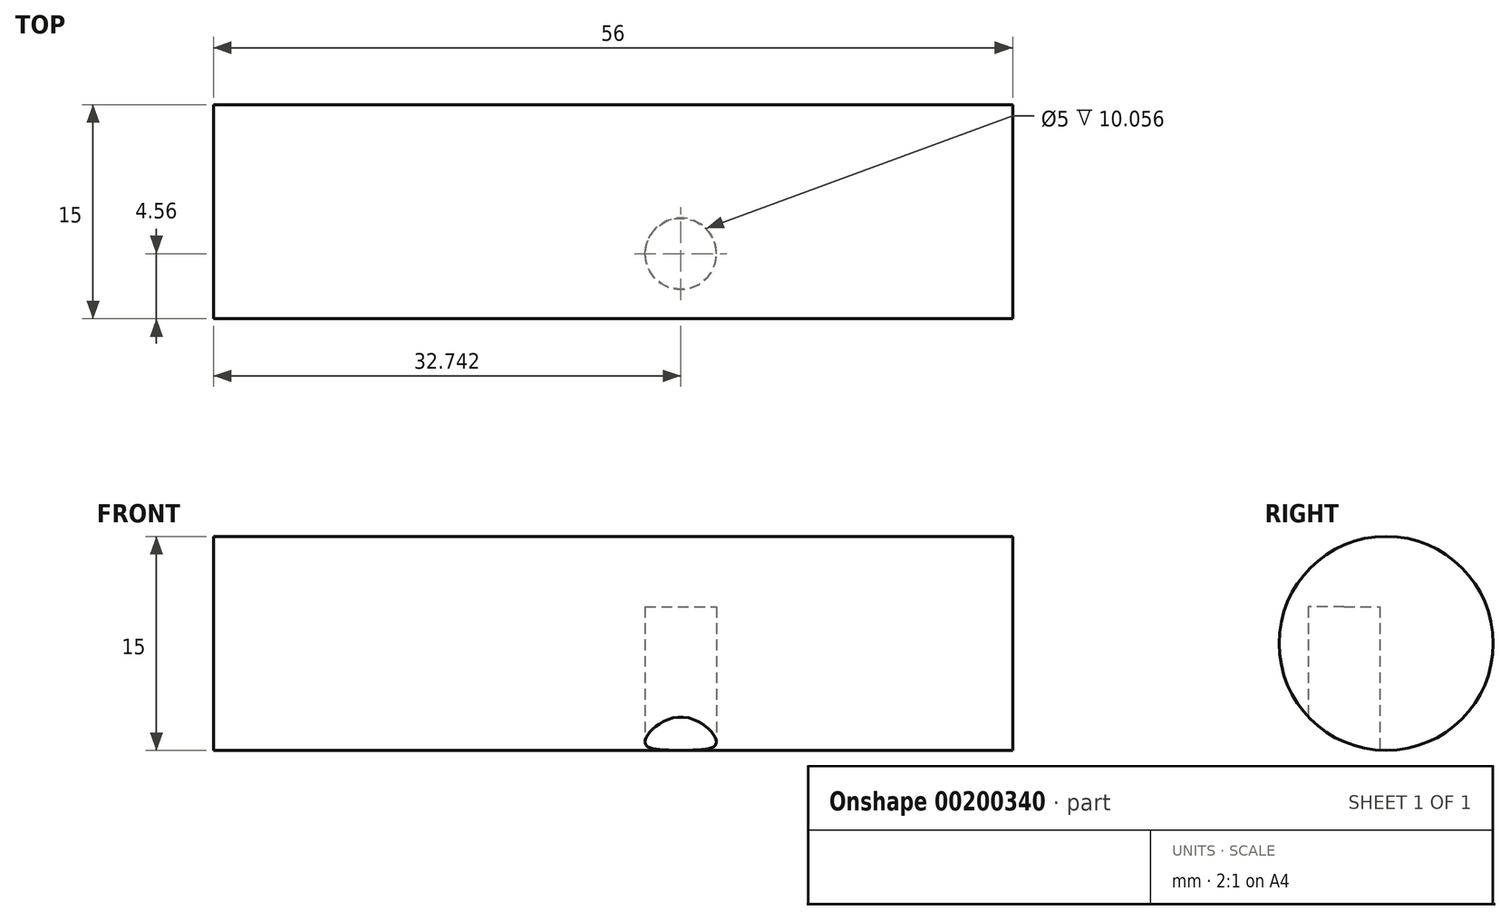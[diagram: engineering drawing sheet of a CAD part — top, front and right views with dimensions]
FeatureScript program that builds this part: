
annotation { "Feature Type Name" : "Feature", "Feature Type Description" : "" }
export const myFeature = defineFeature(function(context is Context, id is Id, definition is map)
    precondition{}
    {
        {
            var Q0;
            Q0=qCreatedBy(makeId("Right.planeOp"),FACE);
            var sketch = newSketch(context, id + "F0", { "sketchPlane" : qUnion([Q0])});
            skCircle(sketch, "E0", {"center": v(-29.89, 17.43) * mm, "radius": 7.5 * mm});
            skSolve(sketch);
        }
        {
            var Q0;
            Q0 = qSketchRegion(id + "F0", true);
            extrude(context, id + "F1", {"entities" : qUnion([Q0]), "depth" : 56 * mm});
        }
        {
            var Q0;
            Q0=qCreatedBy(makeId("Top.planeOp"),FACE);
            var sketch = newSketch(context, id + "F2", { "sketchPlane" : qUnion([Q0])});
            skCircle(sketch, "E1", {"center": v(32.74, -32.83) * mm, "radius": 2.5 * mm});
            skSolve(sketch);
        }
        {
            var Q0;
            Q0 = qSketchRegion(id + "F2", true);
            extrude(context, id + "F3", {"entities" : qUnion([Q0]), "operationType" : NewBodyOperationType.REMOVE, "depth" : 20 * mm});
        }
    });
